# Revit family: Fitting-Ninety_Degree_Angle-Unistrut-P1750
name_source: partatom
category: Specialty Equipment
revit_build: Autodesk Revit MEP 2012 (Build: 20110309_2315(x64)
units: mm (PartAtom-declared; Revit-internal decimal feet)

## types (1)
- P1750
    04 CSI = 26 05 48
    95 CSI = 16070
    Assembly Code = D5020100
    CAD URL = http://unistrut.us
    Default Elevation = 0"
    Hole Diameter = 9/16"
    Literature URL = http://unistrut.us
    Load Capacity Note = Visit the product page for load application and capacity.
    Manufacturer = Unistrut by Atkore International
    Manufacturer Fax = 708-339-7814
    Model = P1750
    Overall Height = 1 5/8"
    Overall Length = 2 5/8"
    Overall Width = 1 5/8"
    Part Type = Fitting
    Power Strut Part Number = PS 2545
    Product Page URL = http://unistrut.us
    Subcategory = Nintey Degree Angle Fittings
    Thickness = 1/4"
    URL = http://unistrut.us
    Unistrut Part Number = P1750
    Unit = <By Category>
    Weight Per Piece = 0.38 lb
    ecoScorecard Product Page = http://products.ecoscorecard.com
    ecoScorecard_data = http://products.ecoscorecard.com

## geometry (parser evidence)
native form markers: Sweep x4
no freeform markers — native parametric forms only
